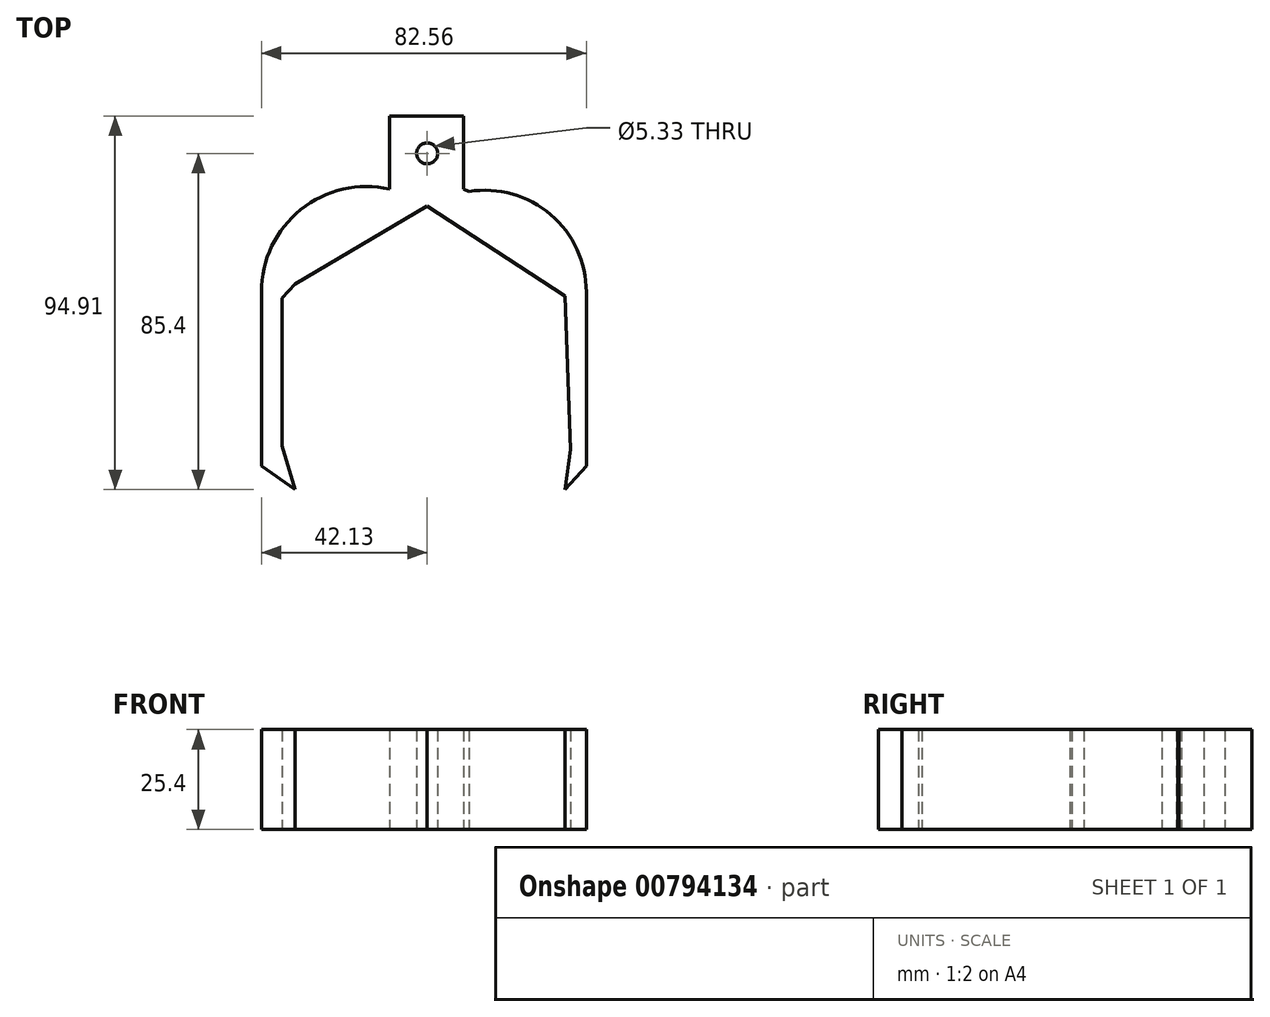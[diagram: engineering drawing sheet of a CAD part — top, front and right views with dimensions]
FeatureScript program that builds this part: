
annotation { "Feature Type Name" : "Feature", "Feature Type Description" : "" }
export const myFeature = defineFeature(function(context is Context, id is Id, definition is map)
    precondition{}
    {
        {
            var Q0;
            Q0=qCreatedBy(makeId("Top.planeOp"),FACE);
            var sketch = newSketch(context, id + "F0", { "sketchPlane" : qUnion([Q0])});
            skLineSegment(sketch, "E0", {"start": v(-42.13, 28.8) * mm, "end": v(-42.13, -15.46) * mm});
            skLineSegment(sketch, "E1", {"start": v(40.43, 28.8) * mm, "end": v(40.43, -15.46) * mm});
            skLineSegment(sketch, "E2", {"start": v(40.43, -15.46) * mm, "end": v(35.04, -21.42) * mm});
            skLineSegment(sketch, "E3", {"start": v(35.04, -21.42) * mm, "end": v(36.46, -11.2) * mm});
            skLineSegment(sketch, "E4", {"start": v(36.46, -11.2) * mm, "end": v(35.04, 27.7) * mm});
            skLineSegment(sketch, "E5", {"start": v(35.04, 27.7) * mm, "end": v(0, 50.56) * mm});
            skLineSegment(sketch, "E6", {"start": v(0, 50.56) * mm, "end": v(-33.59, 30.83) * mm});
            skLineSegment(sketch, "E7", {"start": v(-33.59, 30.83) * mm, "end": v(-36.88, 27.19) * mm});
            skLineSegment(sketch, "E8", {"start": v(-36.88, 27.19) * mm, "end": v(-36.88, -10.33) * mm});
            skLineSegment(sketch, "E9", {"start": v(-36.88, -10.33) * mm, "end": v(-33.59, -21.42) * mm});
            skLineSegment(sketch, "E10", {"start": v(-33.59, -21.42) * mm, "end": v(-42.13, -15.46) * mm});
            skArc(sketch, "E11", {"start": v(-9.54, 54.89) * mm, "mid": v(-32.1, 49.67) * mm, "end": v(-42.13, 28.8) * mm});
            skArc(sketch, "E12", {"start": v(40.43, 28.8) * mm, "mid": v(31.4, 48.42) * mm, "end": v(10.6, 54.3) * mm});
            skLineSegment(sketch, "E13", {"start": v(-9.54, 54.89) * mm, "end": v(-9.54, 73.5) * mm});
            skLineSegment(sketch, "E14", {"start": v(-9.54, 73.5) * mm, "end": v(9.18, 73.5) * mm});
            skLineSegment(sketch, "E15", {"start": v(9.18, 73.5) * mm, "end": v(9.18, 54.89) * mm});
            skLineSegment(sketch, "E16", {"start": v(9.18, 54.89) * mm, "end": v(10.6, 54.3) * mm});
            skCircle(sketch, "E17", {"center": v(0, 63.98) * mm, "radius": 2.66 * mm});
            skSolve(sketch);
        }
        {
            var Q0;
            Q0 = qSketchRegion(id + "F0", true);
            extrude(context, id + "F1", {"entities" : qUnion([Q0]), "depth" : 25.4 * mm, "offsetDistance" : 25.4 * mm});
        }
        {
            var Q0;
            Q0 = qSketchRegion(id + "F0", true);
            extrude(context, id + "F2", {"entities" : qUnion([Q0]), "operationType" : NewBodyOperationType.ADD, "depth" : 25.4 * mm, "offsetDistance" : 25.4 * mm});
        }
    });
